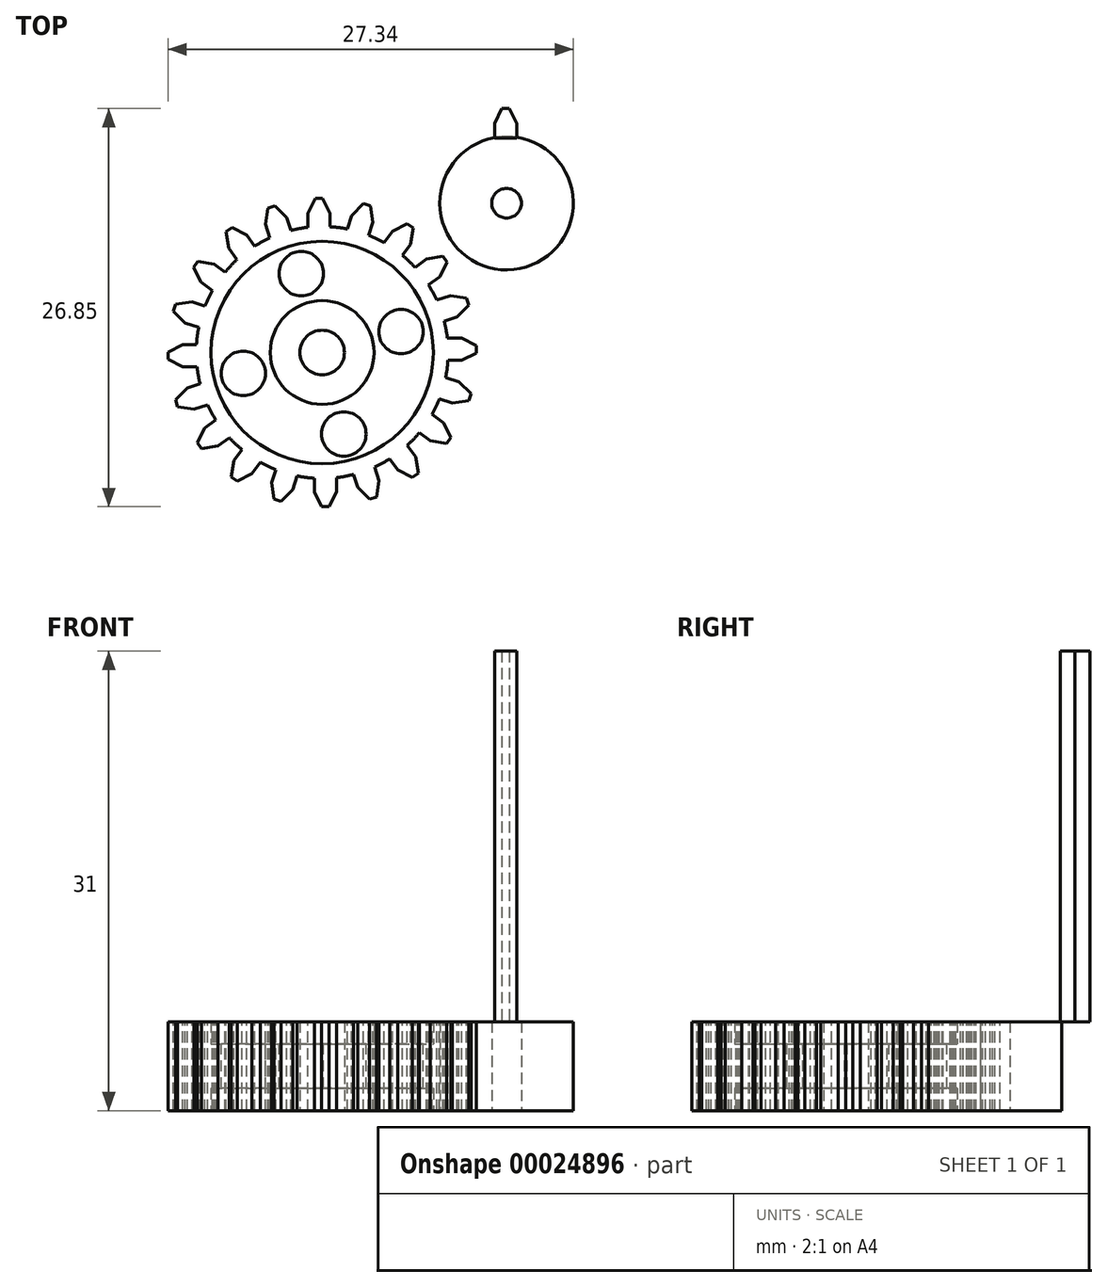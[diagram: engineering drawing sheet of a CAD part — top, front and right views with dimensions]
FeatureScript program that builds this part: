
annotation { "Feature Type Name" : "Feature", "Feature Type Description" : "" }
export const myFeature = defineFeature(function(context is Context, id is Id, definition is map)
    precondition{}
    {
        {
            var Q0;
            Q0=qCreatedBy(makeId("Front.planeOp"),FACE);
            var sketch = newSketch(context, id + "F0", { "sketchPlane" : qUnion([Q0])});
            skLineSegment(sketch, "E0.bottom", {"start": v(-1.5, 0) * mm, "end": v(-8.5, 0) * mm});
            skLineSegment(sketch, "E0.top", {"start": v(-1.5, 6) * mm, "end": v(-8.5, 6) * mm});
            skLineSegment(sketch, "E0.left", {"start": v(-1.5, 0) * mm, "end": v(-1.5, 6) * mm});
            skLineSegment(sketch, "E0.right", {"start": v(-8.5, 0) * mm, "end": v(-8.5, 6) * mm});
            skLineSegment(sketch, "E1.bottom", {"start": v(-3.5, 6) * mm, "end": v(-7.5, 6) * mm});
            skLineSegment(sketch, "E1.top", {"start": v(-3.5, 4.5) * mm, "end": v(-7.5, 4.5) * mm});
            skLineSegment(sketch, "E1.left", {"start": v(-3.5, 6) * mm, "end": v(-3.5, 4.5) * mm});
            skLineSegment(sketch, "E1.right", {"start": v(-7.5, 6) * mm, "end": v(-7.5, 4.5) * mm});
            skLineSegment(sketch, "E2.bottom", {"start": v(-7.5, 0) * mm, "end": v(-3.5, 0) * mm});
            skLineSegment(sketch, "E2.top", {"start": v(-7.5, 1.5) * mm, "end": v(-3.5, 1.5) * mm});
            skLineSegment(sketch, "E2.left", {"start": v(-7.5, 0) * mm, "end": v(-7.5, 1.5) * mm});
            skLineSegment(sketch, "E2.right", {"start": v(-3.5, 0) * mm, "end": v(-3.5, 1.5) * mm});
            skLineSegment(sketch, "E3", {"start": v(0, 0) * mm, "end": v(0, 1.56) * mm, "construction": true});
            skLineSegment(sketch, "E4", {"start": v(0, 1.56) * mm, "end": v(0, 6.1) * mm, "construction": true});
            skSolve(sketch);
        }
        {
            var Q0;
            {var subQ4=sQuery(id+"F0.wireOp",EDGE,"E0.left");Q0=makeQuery(id+"F0.imprint","IMPRINT",FACE,{"disambiguationData":[TD([[makeQuery(id+"F0.imprint","IMPRINT",EDGE,{"derivedFrom":subQ4}),1.0]])]});}
            var Q1;
            Q1=sQuery(id+"F0.wireOp",EDGE,"E4");
            revolve(context, id + "F1", {"entities" : qUnion([Q0]), "axis" : qUnion([Q1]), "revolveType" : RevolveType.FULL});
        }
        {
            var Q0;
            Q0=makeQuery(id+"F1.opRevolve","SWEPT_FACE",FACE,{"disambiguationData":[OSD([sQuery(id+"F0.wireOp",EDGE,"E1.top")])]});
            var sketch = newSketch(context, id + "F2", { "sketchPlane" : qUnion([Q0])});
            skCircle(sketch, "E5", {"center": v(-5.32, -1.41) * mm, "radius": 1.5 * mm});
            skCircle(sketch, "E6", {"center": v(-1.41, 5.32) * mm, "radius": 1.5 * mm});
            skCircle(sketch, "E7", {"center": v(5.32, 1.41) * mm, "radius": 1.5 * mm});
            skCircle(sketch, "E8", {"center": v(1.46, -5.5) * mm, "radius": 1.5 * mm});
            skLineSegment(sketch, "E9", {"start": v(-1.41, 5.32) * mm, "end": v(0, 0) * mm, "construction": true});
            skLineSegment(sketch, "E10", {"start": v(0, 0) * mm, "end": v(-5.32, -1.41) * mm, "construction": true});
            skLineSegment(sketch, "E11", {"start": v(5.32, 1.41) * mm, "end": v(0, 0) * mm, "construction": true});
            skLineSegment(sketch, "E12", {"start": v(1.46, -5.5) * mm, "end": v(0, 0) * mm, "construction": true});
            skSolve(sketch);
        }
        {
            var Q0;
            Q0=makeQuery(id+"F2.imprint","IMPRINT",FACE,{"disambiguationData":[TD([[makeQuery(id+"F2.imprint","IMPRINT",EDGE,{"derivedFrom":sQuery(id+"F2.wireOp",EDGE,"E5")}),1.0]])]});
            var Q1;
            Q1=makeQuery(id+"F2.imprint","IMPRINT",FACE,{"disambiguationData":[TD([[makeQuery(id+"F2.imprint","IMPRINT",EDGE,{"derivedFrom":sQuery(id+"F2.wireOp",EDGE,"E6")}),1.0]])]});
            var Q2;
            Q2=makeQuery(id+"F2.imprint","IMPRINT",FACE,{"disambiguationData":[TD([[makeQuery(id+"F2.imprint","IMPRINT",EDGE,{"derivedFrom":sQuery(id+"F2.wireOp",EDGE,"E7")}),1.0]])]});
            var Q3;
            Q3=makeQuery(id+"F2.imprint","IMPRINT",FACE,{"disambiguationData":[TD([[makeQuery(id+"F2.imprint","IMPRINT",EDGE,{"derivedFrom":sQuery(id+"F2.wireOp",EDGE,"E8")}),1.0]])]});
            extrude(context, id + "F3", {"entities" : qUnion([Q0, Q1, Q2, Q3]), "operationType" : NewBodyOperationType.REMOVE, "oppositeDirection" : true, "depth" : 25 * mm});
        }
        {
            var Q0;
            {var subQ0=sQuery(id+"F0.wireOp",EDGE,"E0.top");Q0=makeQuery(id+"F1.opRevolve","SWEPT_FACE",FACE,{"disambiguationData":[OSD([subQ0]),TDD([makeQuery(id+"F0.imprint","IMPRINT",EDGE,{"disambiguationData":[TD([[makeQuery(id+"F0.imprint","INTERSECT",VERTEX,{"derivedFrom":[subQ0,sQuery(id+"F0.wireOp",EDGE,"E0.right")]}),1.0]])],"derivedFrom":subQ0})])]});}
            var sketch = newSketch(context, id + "F4", { "sketchPlane" : qUnion([Q0])});
            skLineSegment(sketch, "E13", {"start": v(0.03, 10.4) * mm, "end": v(0.53, 9.4) * mm});
            skLineSegment(sketch, "E14.bottom", {"start": v(0.53, 8.4) * mm, "end": v(-0.97, 8.4) * mm});
            skLineSegment(sketch, "E14.left", {"start": v(0.53, 8.4) * mm, "end": v(0.53, 10.4) * mm});
            skLineSegment(sketch, "E15", {"start": v(-0.97, 9.4) * mm, "end": v(-0.47, 10.4) * mm});
            skLineSegment(sketch, "E14.right", {"start": v(-0.97, 8.4) * mm, "end": v(-0.97, 10.4) * mm});
            skLineSegment(sketch, "E14.top", {"start": v(0.53, 10.4) * mm, "end": v(-0.97, 10.4) * mm});
            skSolve(sketch);
        }
        {
            var Q0;
            {var subQ2=sQuery(id+"F4.wireOp",EDGE,"E13");Q0=makeQuery(id+"F4.imprint","IMPRINT",FACE,{"disambiguationData":[TD([[makeQuery(id+"F4.imprint","IMPRINT",EDGE,{"derivedFrom":subQ2}),-1.0]])]});}
            extrude(context, id + "F5", {"entities" : qUnion([Q0]), "oppositeDirection" : true, "depth" : 6 * mm});
        }
        {
            var Q0;
            Q0=makeQuery(id+"F5.opExtrude","SWEPT_BODY",BODY,{"disambiguationData":[OSD([sQuery(id+"F0.wireOp",EDGE,"E0.top"),sQuery(id+"F0.wireOp",EDGE,"E0.right"),sQuery(id+"F4.wireOp",EDGE,"E13"),sQuery(id+"F4.wireOp",EDGE,"E14.left"),sQuery(id+"F4.wireOp",EDGE,"E15"),sQuery(id+"F4.wireOp",EDGE,"E14.right"),sQuery(id+"F4.wireOp",EDGE,"E14.top")])]});
            var Q1;
            Q1=makeQuery(id+"F1.opRevolve","SWEPT_EDGE",EDGE,{"disambiguationData":[OSD([sQuery(id+"F0.wireOp",EDGE,"E0.top"),sQuery(id+"F0.wireOp",EDGE,"E0.left")])]});
            circularPattern(context, id + "F6", {"operationType" : NewBodyOperationType.ADD, "entities" : qUnion([Q0]), "axis" : qUnion([Q1]), "angle" : 360 * degree, "instanceCount" : 20, "oppositeDirection" : true, "equalSpace" : true});
        }
        {
            var Q0;
            Q0=qCreatedBy(makeId("Top.planeOp"),FACE);
            var sketch = newSketch(context, id + "F7", { "sketchPlane" : qUnion([Q0])});
            skCircle(sketch, "E16", {"center": v(12.44, 10.07) * mm, "radius": 1 * mm});
            skCircle(sketch, "E17", {"center": v(12.44, 10.07) * mm, "radius": 4.5 * mm});
            skLineSegment(sketch, "E18.bottom", {"start": v(13.3, 14.48) * mm, "end": v(11.8, 14.48) * mm});
            skSolve(sketch);
        }
        {
            var Q0;
            Q0=sQuery(id+"F7.wireOp",EDGE,"E16");
            var Q1;
            Q1=sQuery(id+"F7.wireOp",EDGE,"E17");
            var Q2;
            Q2=sQuery(id+"F7.wireOp",EDGE,"E18.bottom");
            extrude(context, id + "F8", {"bodyType" : ToolBodyType.SURFACE, "surfaceEntities" : qUnion([Q0, Q1, Q2]), "depth" : 6 * mm});
        }
        {
            var Q0;
            Q0=makeQuery(id+"F7.imprint","IMPRINT",FACE,{"disambiguationData":[TD([[makeQuery(id+"F7.imprint","IMPRINT",EDGE,{"derivedFrom":sQuery(id+"F7.wireOp",EDGE,"E16")}),-1.0]])]});
            extrude(context, id + "F9", {"entities" : qUnion([Q0]), "depth" : 6 * mm});
        }
        {
            var Q0;
            Q0=makeQuery(id+"F9.opExtrude","CAP_FACE",FACE,{"disambiguationData":[OSD([sQuery(id+"F7.wireOp",EDGE,"E16"),sQuery(id+"F7.wireOp",EDGE,"E17")])],"isStart":false});
            var sketch = newSketch(context, id + "F10", { "sketchPlane" : qUnion([Q0])});
            skLineSegment(sketch, "E19", {"start": v(12.63, 16.45) * mm, "end": v(13.13, 15.45) * mm});
            skLineSegment(sketch, "E20.bottom", {"start": v(13.13, 14.45) * mm, "end": v(11.63, 14.45) * mm});
            skLineSegment(sketch, "E20.left", {"start": v(13.13, 14.45) * mm, "end": v(13.13, 15.45) * mm});
            skLineSegment(sketch, "E21", {"start": v(11.63, 15.45) * mm, "end": v(12.13, 16.45) * mm});
            skLineSegment(sketch, "E20.right", {"start": v(11.63, 14.45) * mm, "end": v(11.63, 15.45) * mm});
            skLineSegment(sketch, "E20.top", {"start": v(13.13, 16.45) * mm, "end": v(11.63, 16.45) * mm});
            skLineSegment(sketch, "E22.1.0", {"start": v(-19.08, 4.14) * mm, "end": v(-19.95, 3.64) * mm});
            skLineSegment(sketch, "E22.2.0", {"start": v(5.95, -18.6) * mm, "end": v(6.82, -19.1) * mm});
            skPoint(sketch, "E22.center", {"position": v(0, 0) * mm});
            skSolve(sketch);
        }
        {
            var Q0;
            Q0 = qSketchRegion(id + "F10", true);
            extrude(context, id + "F11", {"entities" : qUnion([Q0]), "operationType" : NewBodyOperationType.ADD, "depth" : 25 * mm});
        }
    });
